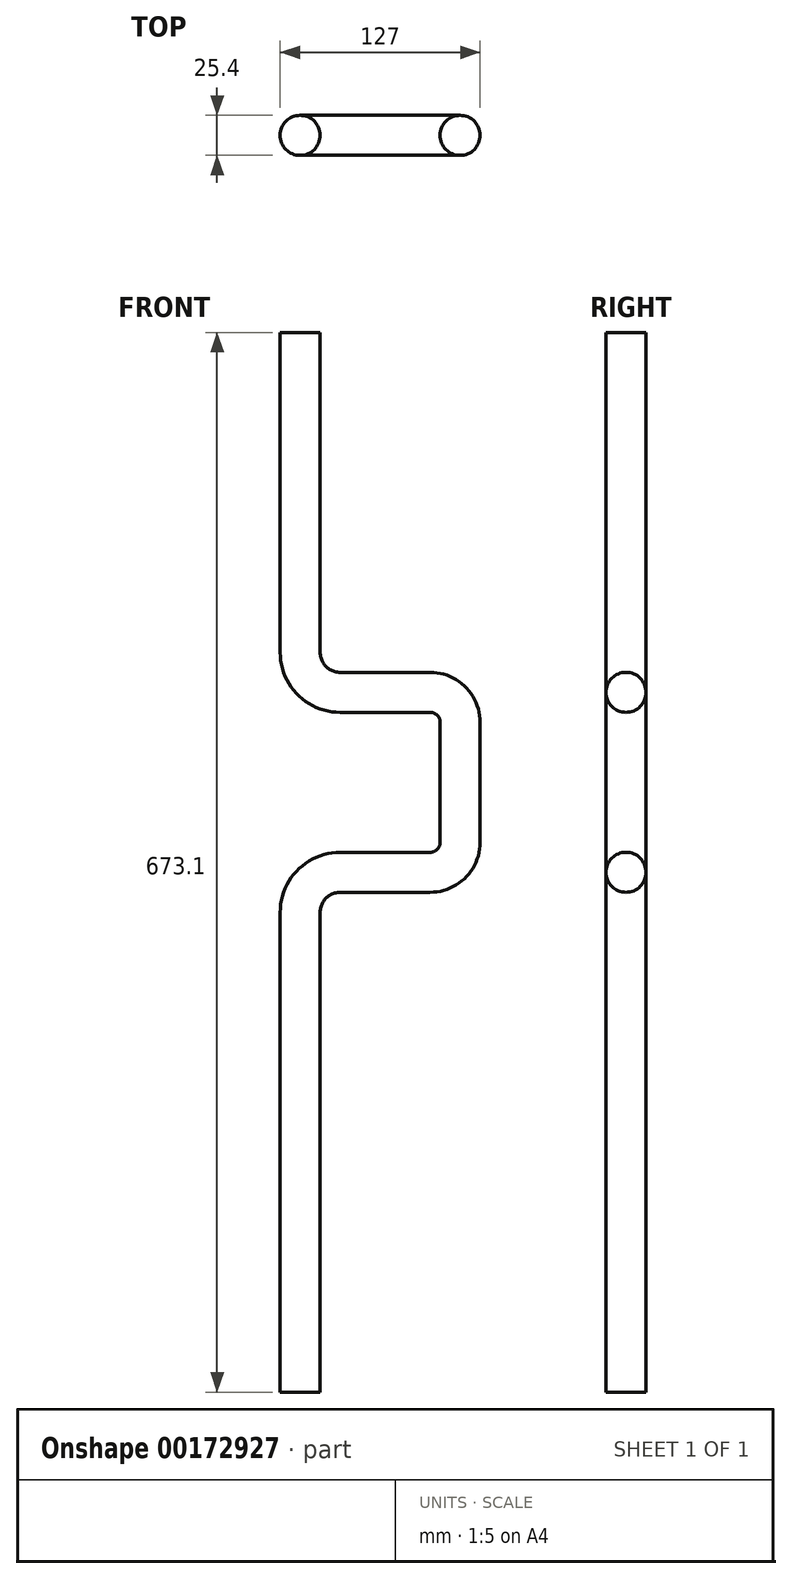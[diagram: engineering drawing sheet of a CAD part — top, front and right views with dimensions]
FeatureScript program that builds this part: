
annotation { "Feature Type Name" : "Feature", "Feature Type Description" : "" }
export const myFeature = defineFeature(function(context is Context, id is Id, definition is map)
    precondition{}
    {
        {
            var Q0;
            Q0=qCreatedBy(makeId("Front.planeOp"),FACE);
            var sketch = newSketch(context, id + "F0", { "sketchPlane" : qUnion([Q0])});
            skLineSegment(sketch, "E0", {"start": v(0, 0) * mm, "end": v(0, 304.8) * mm});
            skArc(sketch, "E1", {"start": v(0, 304.8) * mm, "mid": v(7.44, 322.76) * mm, "end": v(25.4, 330.2) * mm});
            skLineSegment(sketch, "E2", {"start": v(25.4, 330.2) * mm, "end": v(82.55, 330.2) * mm});
            skArc(sketch, "E3", {"start": v(82.55, 330.2) * mm, "mid": v(96.02, 335.78) * mm, "end": v(101.6, 349.25) * mm});
            skLineSegment(sketch, "E4", {"start": v(101.6, 349.25) * mm, "end": v(101.6, 425.45) * mm});
            skArc(sketch, "E5", {"start": v(101.6, 425.45) * mm, "mid": v(96.02, 438.92) * mm, "end": v(82.55, 444.5) * mm});
            skLineSegment(sketch, "E6", {"start": v(82.55, 444.5) * mm, "end": v(25.4, 444.5) * mm});
            skArc(sketch, "E7", {"start": v(25.4, 444.5) * mm, "mid": v(7.44, 451.94) * mm, "end": v(0, 469.9) * mm});
            skLineSegment(sketch, "E8", {"start": v(0, 469.9) * mm, "end": v(0, 673.1) * mm});
            skSolve(sketch);
        }
        {
            var Q0;
            Q0=qCreatedBy(makeId("Top.planeOp"),FACE);
            var sketch = newSketch(context, id + "F1", { "sketchPlane" : qUnion([Q0])});
            skCircle(sketch, "E9", {"center": v(0, 0) * mm, "radius": 12.7 * mm});
            skSolve(sketch);
        }
        {
            var Q0;
            Q0 = qSketchRegion(id + "F1", true);
            var Q1;
            Q1 = qConstructionFilter(qBodyType(qCreatedBy(id + "F0" ,EDGE), BodyType.WIRE), ConstructionObject.NO);
            sweep(context, id + "F2", {"profiles" : qUnion([Q0]), "path" : qUnion([Q1])});
        }
    });
